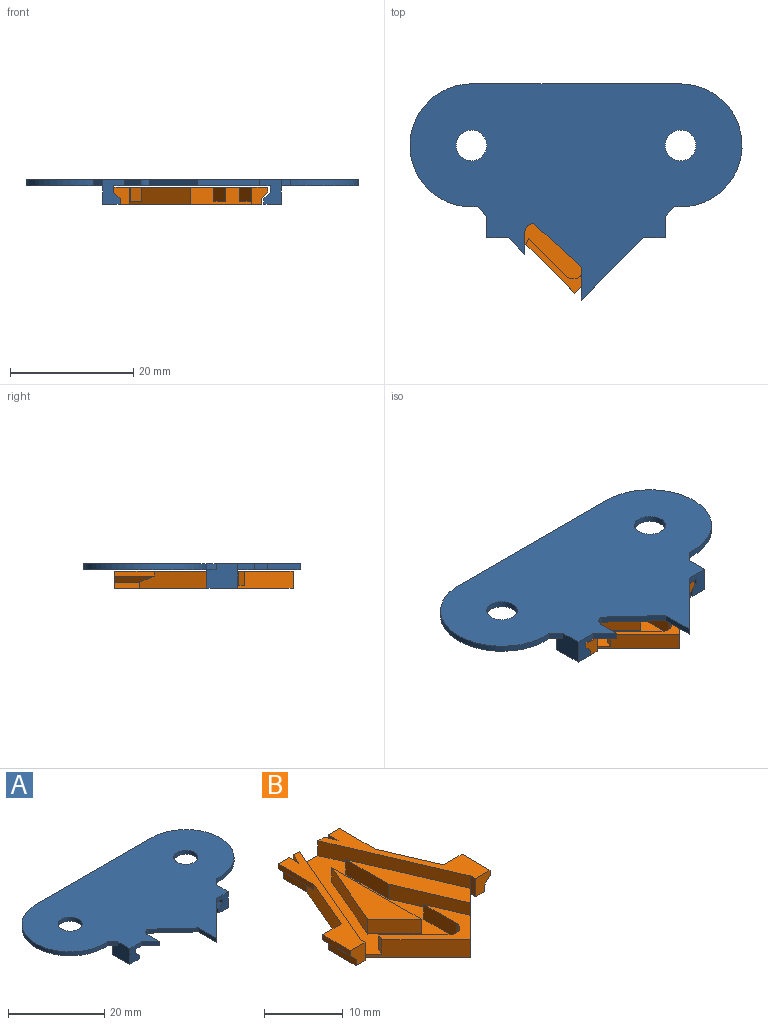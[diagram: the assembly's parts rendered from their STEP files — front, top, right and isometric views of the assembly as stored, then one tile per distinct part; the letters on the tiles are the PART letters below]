
ASSEMBLY  parts=2 mates=1
PART A: 29 faces, bbox 54x35.1x4 mm
  f0: plane 1.54x1.54mm, normal (0.71,-0.71,0), area 2.2mm2, adj f2,f4,f10,f15
  f1: plane 2.69x2.69mm, normal (-0.71,-0.71,0), area 3.8mm2, adj f2,f4,f9,f27
  f2: plane 54x35.14mm, normal (0,0,-1), area 1145.9mm2, adj f0,f1,f3,f5,f6,f7,f8,f9
  f3: plane 1.55x1.55mm, normal (-0.71,-0.71,0), area 2.2mm2, adj f2,f4,f13,f23
  f4: plane 54x35.14mm, normal (0,0,1), area 1163.9mm2, adj f0,f1,f3,f5,f6,f7,f8,f9
  f5: plane 10.14x10.14mm, normal (0.71,-0.71,0), area 14.3mm2, adj f2,f4,f6,f20
  f6: plane 5.36x1mm, normal (-1,0,0), area 5.4mm2, adj f2,f4,f5,f7
  f7: plane 7.7x7.05mm, normal (-0.68,-0.74,0), area 10.4mm2, adj f2,f4,f6,f8
  f8: cylinder r=1.46mm len=1.47mm, axis (0,0,1), area 2.3mm2, adj f2,f4,f7,f9
  f9: plane 3.5x1mm, normal (1,0,0), area 3.5mm2, adj f1,f2,f4,f8
  f10: cylinder r=10mm len=20mm, axis (0,0,1), area 32.4mm2, adj f0,f2,f4,f11
  f11: plane 34.12x1mm, normal (0,1,0), area 34.1mm2, adj f2,f4,f10,f13
  f12: cylinder r=2.5mm len=5mm, axis (0,0,1), area 15.7mm2, adj f2,f4
  f13: cylinder r=10mm len=20mm, axis (0,0,1), area 32.3mm2, adj f2,f3,f4,f11
  f14: cylinder r=2.5mm len=5mm, axis (0,0,1), area 15.7mm2, adj f2,f4
  f15: plane 5x4mm, normal (1,0,0), area 18.5mm2, adj f0,f2,f4,f16,f20,f21
  f16: plane 5x2.8mm, normal (0,0,-1), area 14mm2, adj f15,f17,f20,f21
  f17: plane 5x0.92mm, normal (-1,0,0), area 4.6mm2, adj f16,f18,f20,f21
  f18: plane 5x1mm, normal (-0.71,0,0.71), area 7.1mm2, adj f17,f19,f20,f21
  f19: plane 5x1.08mm, normal (-1,0,0), area 5.4mm2, adj f2,f18,f20,f21
  f20: plane 4x3.5mm, normal (0,-1,0), area 10.3mm2, adj f2,f4,f5,f15,f16,f17,f18,f19
  f21: plane 3x2.8mm, normal (0,1,0), area 6.8mm2, adj f2,f15,f16,f17,f18,f19
  f22: plane 5x2.8mm, normal (0,0,-1), area 14mm2, adj f23,f26,f27,f28
  f23: plane 5x4mm, normal (-1,0,0), area 18.5mm2, adj f2,f3,f4,f22,f27,f28
  f24: plane 5x1.08mm, normal (1,0,0), area 5.4mm2, adj f2,f25,f27,f28
  f25: plane 5x1mm, normal (0.71,0,0.71), area 7.1mm2, adj f24,f26,f27,f28
  f26: plane 5x0.92mm, normal (1,0,0), area 4.6mm2, adj f22,f25,f27,f28
  f27: plane 4x3.5mm, normal (0,-1,0), area 10.3mm2, adj f1,f2,f4,f22,f23,f24,f25,f26
  f28: plane 3x2.8mm, normal (0,1,0), area 6.8mm2, adj f2,f22,f23,f24,f25,f26
PART B: 50 faces, bbox 25x29x2.8 mm
  f0: plane 20x10.84mm, normal (0,0,1), area 41.4mm2, adj f2,f3,f4,f7,f8,f28,f31,f32
  f1: plane 2.8x1.76mm, normal (-0.92,0.39,0), area 5.3mm2, adj f8,f12,f13,f45
  f2: plane 10.9x4.66mm, normal (0.92,0.39,0), area 29.9mm2, adj f0,f13,f32,f40,f41,f43
  f3: plane 2.8x1.76mm, normal (0.92,0.39,0), area 5.3mm2, adj f0,f8,f13,f42
  f4: plane 19.15x8.18mm, normal (-0.92,-0.39,0), area 47.9mm2, adj f0,f5,f7,f8
  f5: plane 26.71x19.69mm, normal (0,0,1), area 212.4mm2, adj f4,f6,f7,f8,f14,f15,f16,f17
  f6: plane 9.9x9.9mm, normal (-0.71,-0.71,0), area 33mm2, adj f5,f7,f10,f12,f13,f24,f25,f39
  f7: plane 9.9x9.9mm, normal (0.71,-0.71,0), area 26.8mm2, adj f0,f4,f5,f6,f9,f10,f13,f20
  f8: plane 5.5x2.8mm, normal (0,1,0), area 7.8mm2, adj f0,f1,f3,f4,f5,f12,f13,f24
  f9: plane 17.95x6.69mm, normal (0,0,1), area 42.4mm2, adj f7,f21,f22,f23
  f10: plane 11.69x9.6mm, normal (0,0,1), area 24.3mm2, adj f6,f7,f17,f18,f19,f20,f25
  f11: plane 10.9x4.66mm, normal (-0.92,0.39,0), area 29.9mm2, adj f12,f13,f37,f46,f47,f48
  f12: plane 20x10.84mm, normal (0,0,1), area 41.4mm2, adj f1,f6,f8,f11,f24,f34,f36,f37
  f13: plane 29x23mm, normal (0,0,-1), area 379.6mm2, adj f1,f2,f3,f6,f7,f8,f11,f30
  f14: plane 11.29x4.82mm, normal (-0.92,0.39,0), area 28.2mm2, adj f5,f15,f26,f27
  f15: plane 15.99x2.3mm, normal (1,0,0), area 36.8mm2, adj f5,f14,f16,f27
  f16: plane 4.76x4.76mm, normal (-0.71,-0.71,0), area 15.5mm2, adj f5,f15,f26,f27
  f17: plane 6.21x6.21mm, normal (0.71,0.71,0), area 20.2mm2, adj f5,f10,f18,f25
  f18: cylinder r=1.5mm len=2.56mm, axis (0,0,1), area 8.1mm2, adj f5,f10,f17,f19
  f19: plane 5.81x2.3mm, normal (-1,0,0), area 13.4mm2, adj f5,f10,f18,f20
  f20: plane 5.85x2.5mm, normal (0.92,0.39,0), area 14.6mm2, adj f5,f7,f10,f19
  f21: plane 10.31x4.4mm, normal (-0.92,-0.39,0), area 25.8mm2, adj f5,f7,f9,f22
  f22: plane 7.64x2.3mm, normal (-1,0,0), area 17.6mm2, adj f5,f9,f21,f23
  f23: plane 15.66x6.69mm, normal (0.92,0.39,0), area 39.2mm2, adj f5,f7,f9,f22
  f24: plane 19.15x8.18mm, normal (0.92,-0.39,0), area 47.9mm2, adj f5,f6,f8,f12
  f25: plane 2.3x0.99mm, normal (-0.92,0.39,0), area 2.5mm2, adj f5,f6,f10,f17
  f26: plane 2.3x0.06mm, normal (0.71,-0.71,0), area 0.2mm2, adj f5,f14,f16,f27
  f27: plane 15.99x4.82mm, normal (0,0,1), area 38.2mm2, adj f14,f15,f16,f26
  f28: plane 5x0.8mm, normal (1,0,0), area 4mm2, adj f0,f29,f31,f32
  f29: plane 5x1mm, normal (0.71,0,-0.71), area 7.1mm2, adj f28,f30,f31,f32
  f30: plane 5x1mm, normal (1,0,0), area 5mm2, adj f13,f29,f31,f32
  f31: plane 2.8x2.6mm, normal (0,-1,0), area 5.8mm2, adj f0,f13,f28,f29,f30,f38
  f32: plane 3.34x2.8mm, normal (0,1,0), area 7.9mm2, adj f0,f2,f13,f28,f29,f30
  f33: plane 5x1mm, normal (-0.71,0,-0.71), area 7.1mm2, adj f34,f35,f36,f37
  f34: plane 5x0.8mm, normal (-1,0,0), area 4mm2, adj f12,f33,f36,f37
  f35: plane 5x1mm, normal (-1,0,0), area 5mm2, adj f13,f33,f36,f37
  f36: plane 2.8x2.6mm, normal (0,-1,0), area 5.8mm2, adj f12,f13,f33,f34,f35,f39
  f37: plane 3.34x2.8mm, normal (0,1,0), area 7.9mm2, adj f11,f12,f13,f33,f34,f35
  f38: plane 2.8x0.9mm, normal (-1,0,0), area 2.5mm2, adj f0,f7,f13,f31
  f39: plane 2.8x0.9mm, normal (1,0,0), area 2.5mm2, adj f6,f12,f13,f36
  f40: plane 6.44x1mm, normal (0.71,0,-0.71), area 7.4mm2, adj f2,f41,f43,f44
  f41: plane 4.1x1mm, normal (1,0,0), area 4.1mm2, adj f2,f13,f40,f44
  f42: plane 2.8x1.76mm, normal (-1,0,0), area 4.9mm2, adj f0,f3,f13,f44
  f43: plane 6.44x0.8mm, normal (1,0,0), area 5.2mm2, adj f0,f2,f40,f44
  f44: plane 2.8x2mm, normal (0,1,0), area 4.1mm2, adj f0,f13,f40,f41,f42,f43
  f45: plane 2.8x1.76mm, normal (1,0,0), area 4.9mm2, adj f1,f12,f13,f49
  f46: plane 4.1x1mm, normal (-1,0,0), area 4.1mm2, adj f11,f13,f47,f49
  f47: plane 6.44x1mm, normal (-0.71,0,-0.71), area 7.4mm2, adj f11,f46,f48,f49
  f48: plane 6.44x0.8mm, normal (-1,0,0), area 5.2mm2, adj f11,f12,f47,f49
  f49: plane 2.8x2mm, normal (0,1,0), area 4.1mm2, adj f12,f13,f45,f46,f47,f48
PLACE A rot(axis=(0,0,-1),0deg) t=(-5.81,33,-8.86)mm
PLACE B t=(-6.01,-16.25,-8.86)mm
MATE fastened A.f26 <-> B.f35  axis (1,0,0) through (-17.51,-2.25,-11.86)mm
